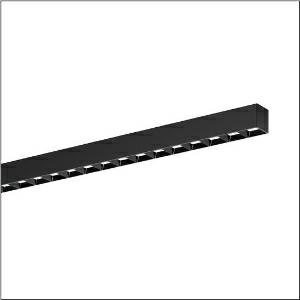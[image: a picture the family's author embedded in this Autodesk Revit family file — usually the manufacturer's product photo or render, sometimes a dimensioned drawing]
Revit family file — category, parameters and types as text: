
# Revit family: silica_r__21_51mx22dc3abb_349a
name_source: partatom
category: Lighting Fixtures
units: mm (PartAtom-declared; Revit-internal decimal feet)

## family parameters
Cut with Voids When Loaded = No
Host = Face
Light Source = No
Part Type = Normal
Room Calculation Point = No
Round Connector Dimension = Use Diameter
Shared = No

## types (1)
- --- (1 x LED, 10800 lm, 69.2 W, 3000K)
    Apparent Load = 69 VA
    CIE Flux Codes = 86 100 100 100 100
    Color Rendering = 80
    Color Temperature = 3000K
    Default Elevation = 1800 mm
    Description = Silica® 21, office luminaire, primary light control with darklight reflector, of PMMA, black, CAT 2 (L<= 3000cd/m²), light emission: direct distribution, primary light characteristic: symmetric, installation type: surface-mounted, LED, rated luminous flux: 10.800lm, luminous efficacy: 156lm/W, light colour: 830, colour temperature: 3000K, control gear: DALI 2, with terminal, 3+2-pole, max. 2.5mm², mains connection: 220..240V, AC, 50/60Hz, rated input power: 69.2W, luminaire housing, of aluminium, matt jet black (RAL 9005), length: 3.004mm, width: 53mm, height: 53mm, protection rating (complete): IP20, insulation class (complete): insulation class I (protective earthing), certification: CE, permissible operating ambient temperature: 0..+35°C, standard: EN 50419, packaging unit: 1 piece
    Height = 53 mm
    Lamp = 1 x LED
    Lamp Light Flux = 10800 lm
    Lamp Power = 69.2 W
    Lamp count = 1
    Length = 3004 mm
    Luminous efficacy = 156 lm/W
    Manufacturer = Siteco
    ModVariant = No
    Model = 51MX22DC3ABB
    Mounting Place = Ceiling
    Mounting Type = Surface mounted
    Number of Poles = 1
    OnlyDefault = Yes
    Power Factor = 1
    Product Name = Silica® 21
    Product group = office luminaire | ceiling mounted
    ProductGroupID = 302
    Protection Class = Protection class I
    Protection Degree = IP 20
    RLX_Detail_Level = 1
    RLX_Emergency_Light_Flux = 0 lm
    RLX_Emergency_Type = 0
    RLX_Emergency_Type_DB = No
    RlxData = <blob elided: 64549 chars, md5=a8d743da>
    Socket = socket
    Standby Power = 0 W
    System Light Flux = 10800 lm
    System Power = 69 W
    Type Comments = factory setting: luminous flux: 100 % | dim-lin: 254 | 392 mA
    Type Image = l_1335908.jpg
    URL = http://relux.com
    VarID = @adj_124672
    Voltage = 0 V
    Weight = 0.00 kg
    Width = 53 mm

## geometry (parser evidence)
native form markers: Blend x4, Sweep x9
no freeform markers — native parametric forms only
